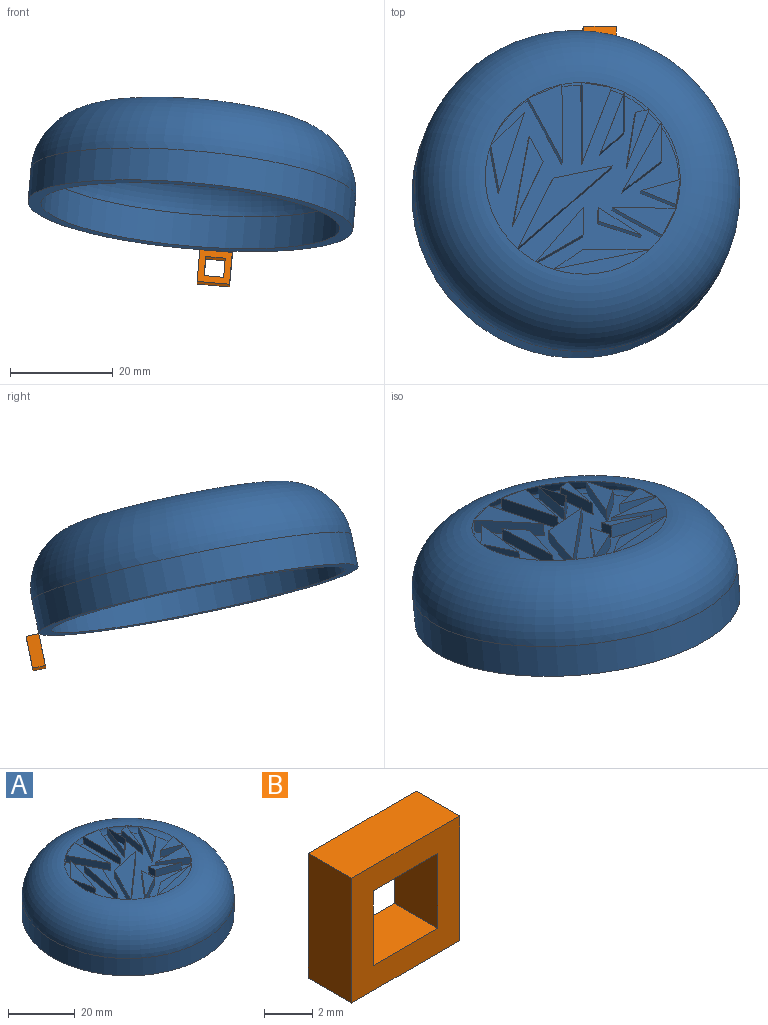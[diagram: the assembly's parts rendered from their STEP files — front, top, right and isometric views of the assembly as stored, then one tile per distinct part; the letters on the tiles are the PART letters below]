
ASSEMBLY  parts=2 mates=1
PART A: 54 faces, bbox 68.7x68.7x19.1 mm
  f0: plane 38.1x37.18mm, normal (0,0,1), area 692.5mm2, adj f12,f15,f16,f17,f19,f20,f21,f22
  f1: plane 5.43x2.74mm, normal (0,0,1), area 1mm2, adj f12,f24
  f2: plane 5.81x0.91mm, normal (0,0,1), area 0.9mm2, adj f12,f28
  f3: plane 18.72x5.01mm, normal (0,0,1), area 33.5mm2, adj f12,f23
  f4: plane 6.6x2.76mm, normal (0,0,1), area 1.6mm2, adj f12,f18
  f5: plane 38.1x37.18mm, normal (0,0,-1), area 692.5mm2, adj f14,f15,f16,f17,f19,f20,f21,f22
  f6: plane 5.43x2.74mm, normal (0,0,-1), area 1mm2, adj f14,f24
  f7: plane 5.81x0.91mm, normal (0,0,-1), area 0.9mm2, adj f14,f28
  f8: plane 18.72x5.01mm, normal (0,0,-1), area 33.5mm2, adj f14,f23
  f9: plane 6.6x2.76mm, normal (0,0,-1), area 1.6mm2, adj f14,f18
  f10: cylinder r=31.75mm len=63.5mm, axis (0,0,-1), area 1266.8mm2, adj f11,f12
  f11: plane 63.5x63.5mm, normal (0,0,-1), area 486.4mm2, adj f10,f13
  f12: torus R=19.05mm, axis (0,0,1), area 3401.2mm2, adj f0,f1,f2,f3,f4,f10
  f13: cylinder r=29.21mm len=58.42mm, axis (0,0,-1), area 1165.4mm2, adj f11,f14
  f14: torus R=19.05mm, axis (0,0,1), area 2558.8mm2, adj f5,f6,f7,f8,f9,f13
  f15: plane 11.63x2.54mm, normal (0.21,-0.98,0), area 30.2mm2, adj f0,f5,f16,f17
  f16: plane 18.69x16.58mm, normal (-0.66,0.75,0), area 63.5mm2, adj f0,f5,f15,f17
  f17: plane 14.04x7.06mm, normal (0.89,-0.45,0), area 39.9mm2, adj f0,f5,f15,f16
  f18: plane 6.6x2.76mm, normal (0.39,-0.92,0), area 18.2mm2, adj f4,f9,f19,f20
  f19: plane 12.58x6.6mm, normal (0.89,0.46,0), area 36.1mm2, adj f0,f5,f18,f20
  f20: plane 15.34x2.54mm, normal (-1,0,0), area 39mm2, adj f0,f5,f18,f19
  f21: plane 12.87x2.54mm, normal (0,-1,0), area 32.7mm2, adj f0,f5,f22,f23
  f22: plane 5.85x4.09mm, normal (0.57,-0.82,0), area 18.1mm2, adj f0,f5,f21,f23
  f23: plane 18.72x4.09mm, normal (-0.21,0.98,0), area 48.7mm2, adj f3,f8,f21,f22
  f24: plane 5.43x2.74mm, normal (-0.89,0.45,0), area 15.4mm2, adj f1,f6,f25,f26
  f25: plane 12.35x2.54mm, normal (0,-1,0), area 31.4mm2, adj f0,f5,f24,f26
  f26: plane 9.61x5.43mm, normal (0.49,0.87,0), area 28mm2, adj f0,f5,f24,f25
  f27: plane 14.84x5.81mm, normal (-0.93,0.36,0), area 40.5mm2, adj f0,f5,f28,f29
  f28: plane 5.81x2.54mm, normal (-0.15,-0.99,0), area 14.9mm2, adj f2,f7,f27,f29
  f29: plane 15.75x2.54mm, normal (1,0,0), area 40mm2, adj f0,f5,f27,f28
  f30: plane 4.72x4.17mm, normal (-0.66,0.75,0), area 16mm2, adj f0,f5,f31,f32
  f31: plane 7.88x2.54mm, normal (-1,0,0), area 20mm2, adj f0,f5,f30,f32
  f32: plane 12.05x4.72mm, normal (0.93,-0.36,0), area 32.9mm2, adj f0,f5,f30,f31
  f33: plane 10.71x2.54mm, normal (0.99,-0.16,0), area 27.6mm2, adj f0,f5,f34,f35
  f34: plane 11.29x4.42mm, normal (-0.93,0.36,0), area 30.8mm2, adj f0,f5,f33,f35
  f35: plane 2.65x2.54mm, normal (0.21,-0.98,0), area 6.9mm2, adj f0,f5,f33,f34
  f36: plane 17.5x3.3mm, normal (0.98,-0.19,0), area 45.2mm2, adj f0,f5,f37,f38
  f37: plane 12.53x5.91mm, normal (-0.9,0.43,0), area 35.2mm2, adj f0,f5,f36,f38
  f38: plane 4.97x2.61mm, normal (-0.89,-0.46,0), area 14.3mm2, adj f0,f5,f36,f37
  f39: plane 15.54x5.06mm, normal (-0.95,0.31,0), area 41.5mm2, adj f0,f5,f40,f41
  f40: plane 8.96x2.54mm, normal (0.98,0.17,0), area 23.1mm2, adj f0,f5,f39,f41
  f41: plane 6.64x6.58mm, normal (0.7,-0.71,0), area 23.7mm2, adj f0,f5,f39,f40
  f42: plane 5.43x2.54mm, normal (-1,0,0), area 13.8mm2, adj f0,f5,f43,f44
  f43: plane 10.89x9.27mm, normal (0.76,-0.65,0), area 36.3mm2, adj f0,f5,f42,f44
  f44: plane 9.27x5.46mm, normal (-0.51,0.86,0), area 27.3mm2, adj f0,f5,f42,f43
  f45: plane 2.71x2.54mm, normal (1,0,0), area 6.9mm2, adj f0,f5,f46,f47
  f46: plane 8.32x2.71mm, normal (0.31,0.95,0), area 22.2mm2, adj f0,f5,f45,f47
  f47: plane 8.32x5.43mm, normal (-0.55,-0.84,0), area 25.2mm2, adj f0,f5,f45,f46
  f48: plane 6.79x2.66mm, normal (0.36,0.93,0), area 18.5mm2, adj f0,f5,f49,f50
  f49: plane 4.97x2.54mm, normal (-0.98,0.18,0), area 12.8mm2, adj f0,f5,f48,f50
  f50: plane 7.68x2.54mm, normal (0.29,-0.96,0), area 20.4mm2, adj f0,f5,f48,f49
  f51: plane 7.62x5.92mm, normal (-0.61,0.79,0), area 24.5mm2, adj f0,f5,f52,f53
  f52: plane 7.58x2.54mm, normal (-1,0,0), area 19.2mm2, adj f0,f5,f51,f53
  f53: plane 13.49x7.62mm, normal (0.87,-0.49,0), area 39.4mm2, adj f0,f5,f51,f52
PART B: 10 faces, bbox 6.4x2.5x6.4 mm
  f0: plane 6.35x2.54mm, normal (0,0,1), area 16.1mm2, adj f1,f3,f4,f5
  f1: plane 6.35x2.54mm, normal (-1,0,0), area 16.1mm2, adj f0,f2,f4,f5
  f2: plane 6.35x2.54mm, normal (0,0,-1), area 16.1mm2, adj f1,f3,f4,f5
  f3: plane 6.35x2.54mm, normal (1,0,0), area 16.1mm2, adj f0,f2,f4,f5
  f4: plane 6.35x6.35mm, normal (0,-1,0), area 25.8mm2, adj f0,f1,f2,f3,f6,f7,f8,f9
  f5: plane 6.35x6.35mm, normal (0,1,0), area 25.8mm2, adj f0,f1,f2,f3,f6,f7,f8,f9
  f6: plane 3.81x2.54mm, normal (1,0,0), area 9.7mm2, adj f4,f5,f7,f9
  f7: plane 3.81x2.54mm, normal (0,0,1), area 9.7mm2, adj f4,f5,f6,f8
  f8: plane 3.81x2.54mm, normal (-1,0,0), area 9.7mm2, adj f4,f5,f7,f9
  f9: plane 3.81x2.54mm, normal (0,0,-1), area 9.7mm2, adj f4,f5,f6,f8
PLACE A rot(axis=(-0.92,0.39,0),12.7deg) t=(35.62,-47.47,-32.29)mm
PLACE B rot(axis=(-0.92,0.39,-0.04),12.7deg) t=(36.91,-15.21,-45.6)mm
MATE planar A.f10 <-> B.f0  axis (-0.09,-0.2,-0.98) through (35.62,-47.47,-32.29)mm
